# Revit family: QF_Vollrath-VBBE1-37T
name_source: partatom
category: Specialty Equipment
revit_build: Autodesk Revit 2018 (Build: 20190510_1515(x64)
units: mm (PartAtom-declared; Revit-internal decimal feet)

## family parameters
Always vertical = Yes
Cut with Voids When Loaded = Yes
Part Type = Normal
Room Calculation Point = No
Round Connector Dimension = Use Diameter
Shared = No
Work Plane-Based = No

## types (2) — shared parameters
Apparent Power = 0 VA
BTUH = 1520.0 Btu/h
Conn Plug = NEMA 5-15P
Cycle = 60 Hz
Description = 5.28 Gallon Refrigerated Beverage Dispenser
Elec Conn RI Height = 0"
FL Amps = 3 A
Foodservice Equipment Identifier = Yes
HP = -
Manufacturer = Vollrath
Phase = 1
Refrigerant Type = R134a
Volts = 115 V
Watts = 0 W
Weight in Pounds = 39.7
zero-valued in all types: Cost

## type names (no varying parameters)
- VBBE1-37-S
- VBBE1-37-F

note: column(s) folded — value = type name in every type: Model

## geometry (parser evidence)
native form markers: Blend x2, Sweep x2
no freeform markers — native parametric forms only
